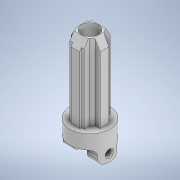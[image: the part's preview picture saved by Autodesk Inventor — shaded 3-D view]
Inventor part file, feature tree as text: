
AUTODESK INVENTOR PART (.ipt)
format: ipt  version: 2022 (Build 260153000, 153)  size: 318,976 bytes
history: native  units: in
note: dims shown in document units (in); Inventor stores cm internally (conversion verified against a paired STEP export)
features: sketch x7, extrude x6, chamfer x2, pattern_circular x1, fillet x1, hole x1
ambient origin geometry x8: Origin, YZ Plane, XZ Plane, XY Plane, X Axis, Y Axis, Z Axis, Center Point
bodies: Solid1 (feature_tree)
feature tree (18):
  extrude  "Extrusion1"  Depth=0.1969in TaperAngle=0.0deg
  extrude  "Extrusion2"  Depth=0.2756in TaperAngle=0.0deg
  extrude  "Extrusion3"  Depth=1.5748in TaperAngle=360.0deg
  extrude  "Extrusion4"  Depth=0.2717in
  extrude  "Extrusion5"  Depth=0.7874in TaperAngle=360.0deg
  pattern_circular  "Circular Pattern1"  [2 undecoded]
  fillet  "Fillet2"  Radius=0.1358in
  hole  "Hole2"  [1 undecoded]
  chamfer  "Chamfer2"  Distance=0.0197in Angle=45.0deg
  chamfer  "Chamfer3"  Distance=0.2953in
  extrude  "Extrusion6"  Depth=0.122in
  sketch  "Sketch1"  dims[d0=0.5512in d2=0.1969in d3=0.0in]
  sketch  "Sketch2"  dims[d13=1.063in d14=0.0in d17=0.2756in d18=0.0in]
  sketch  "Sketch3"  dims[d26=0.0787in d27=1.5748in d29=360.0deg]
  sketch  "Sketch4"  dims[d31=0.0787in d32=0.0in d33=0.2717in]
  sketch  "Sketch5"  dims[d34=0.1969in d35=0.0in d47=0.7874in d48=360.0deg]
  sketch  "Sketch7"  dims[d50=0.1772in]
  sketch  "Sketch9"  dims[d51=0.0787in d52=0.0984in d53=0.1358in d54=0.0787in d55=0.2362in d56=0.1575in d57=0.0787in d58=90.0deg d59=0.315in d60=0.8108in d61=0.2362in d62=0.0197in d63=0.0787in d64=45.0deg d65=0.2953in d67=0.122in d68=0.1102in d69=1.5748in d71=360.0deg d75=0.2008in d76=0.0236in d78=0.7874in d80=360.0deg d82=0.0787in d83=0.0787in d84=60.0deg d85=0.1969in d86=0.0in d88=0.1004in d90=0.0925in]
note: 3 required parameter values undecoded (feature->parameter linkage not recoverable at this tier; creation-order binding heuristic only, values carry confidence <= 0.55)
